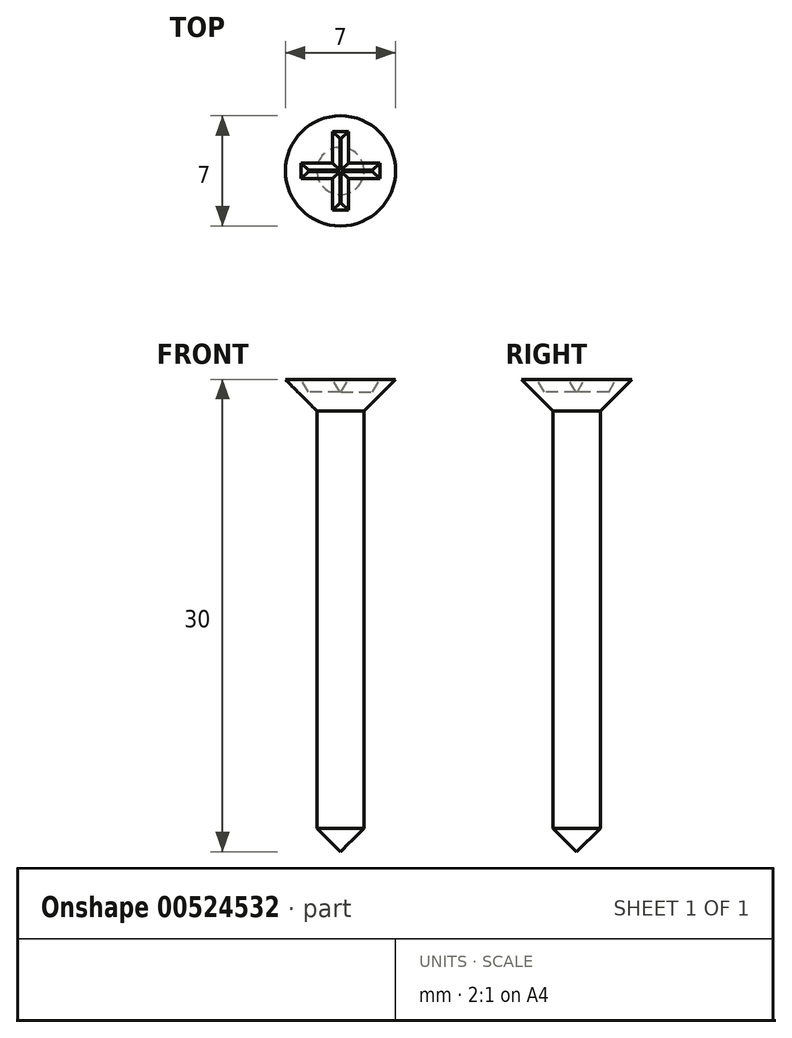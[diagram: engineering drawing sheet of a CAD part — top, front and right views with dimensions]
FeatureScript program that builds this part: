
annotation { "Feature Type Name" : "Feature", "Feature Type Description" : "" }
export const myFeature = defineFeature(function(context is Context, id is Id, definition is map)
    precondition{}
    {
        {
            var Q0;
            Q0=qCreatedBy(makeId("Front.planeOp"),FACE);
            var sketch = newSketch(context, id + "F0", { "sketchPlane" : qUnion([Q0])});
            skLineSegment(sketch, "E0", {"start": v(0, 0) * mm, "end": v(0, 30) * mm});
            skLineSegment(sketch, "E1", {"start": v(0, 30) * mm, "end": v(3.5, 30) * mm});
            skLineSegment(sketch, "E2", {"start": v(3.5, 30) * mm, "end": v(1.5, 28) * mm});
            skLineSegment(sketch, "E3", {"start": v(1.5, 28) * mm, "end": v(1.5, 1.5) * mm});
            skLineSegment(sketch, "E4", {"start": v(1.5, 1.5) * mm, "end": v(0, 0) * mm});
            skSolve(sketch);
        }
        {
            var Q0;
            Q0 = qSketchRegion(id + "F0", true);
            var Q1;
            Q1=sQuery(id+"F0.wireOp",EDGE,"E0");
            revolve(context, id + "F1", {"entities" : qUnion([Q0]), "axis" : qUnion([Q1]), "revolveType" : RevolveType.FULL});
        }
        {
            var Q0;
            Q0=makeQuery(id+"F1.opRevolve","SWEPT_FACE",FACE,{"disambiguationData":[OSD([sQuery(id+"F0.wireOp",EDGE,"E1")])]});
            var sketch = newSketch(context, id + "F2", { "sketchPlane" : qUnion([Q0])});
            skLineSegment(sketch, "E5", {"start": v(-0.5, 2.5) * mm, "end": v(0.5, 2.5) * mm});
            skLineSegment(sketch, "E6", {"start": v(0.5, 2.5) * mm, "end": v(0.5, 0.5) * mm});
            skLineSegment(sketch, "E7", {"start": v(0.5, 0.5) * mm, "end": v(2.5, 0.5) * mm});
            skLineSegment(sketch, "E8", {"start": v(2.5, 0.5) * mm, "end": v(2.5, -0.5) * mm});
            skLineSegment(sketch, "E9", {"start": v(2.5, -0.5) * mm, "end": v(0.5, -0.5) * mm});
            skLineSegment(sketch, "E10", {"start": v(0.5, -0.5) * mm, "end": v(0.5, -2.5) * mm});
            skLineSegment(sketch, "E11", {"start": v(0.5, -2.5) * mm, "end": v(-0.5, -2.5) * mm});
            skLineSegment(sketch, "E12", {"start": v(-0.5, -2.5) * mm, "end": v(-0.5, -0.5) * mm});
            skLineSegment(sketch, "E13", {"start": v(-0.5, -0.5) * mm, "end": v(-2.5, -0.5) * mm});
            skLineSegment(sketch, "E14", {"start": v(-2.5, -0.5) * mm, "end": v(-2.5, 0.5) * mm});
            skLineSegment(sketch, "E15", {"start": v(-2.5, 0.5) * mm, "end": v(-0.5, 0.5) * mm});
            skLineSegment(sketch, "E16", {"start": v(-0.5, 0.5) * mm, "end": v(-0.5, 2.5) * mm});
            skSolve(sketch);
        }
        {
            var Q0;
            Q0 = qSketchRegion(id + "F2", true);
            extrude(context, id + "F3", {"entities" : qUnion([Q0]), "operationType" : NewBodyOperationType.REMOVE, "oppositeDirection" : true, "depth" : 0.8 * mm, "offsetDistance" : 25 * mm, "hasDraft" : true, "draftAngle" : 30 * degree, "draftPullDirection" : true});
        }
    });
